# Revit family: AMB 162(182)_RFA_1
name_source: partatom
category: Pipe Accessories
units: mm (PartAtom-declared; Revit-internal decimal feet)

## family parameters
Always vertical = Yes
Cut with Voids When Loaded = No
OmniClass Number = 23.65.55.14.17
OmniClass Title = Adjusting/Controlling Valves for Liquid Services
Part Type = Normal
Round Connector Dimension = Use Diameter
Shared = Yes
Work Plane-Based = No

## types (22) — shared parameters
Body Material = Danfoss Plastic Dark Gray
Description = Gear Actuator
H = 101 mm  [stored 0.331365 ft]
IfcExportAs = IfcActuatorType
IfcExportType = AMB Actuator
L = 101 mm  [stored 0.331365 ft]
Manufacturer = Danfoss
Max Ambient Temperature = 50 °C
Max Medium Temperature = 110 °C
Min Ambient Temperature = 0 °C
URL = https://store.danfoss.com
W = 84 mm  [stored 0.275591 ft]

## per-type parameters (varying)
| type | Control Input Signal | For Rotary Valve DN | Model | Model Type | Operating Torque | Speed | Weight | With Auxiliary Switch |
| AMB 162_2-point_24V_15s/°_082H0270_082H0272 | 2-point | DN15-50 | 082H0270, 082H0272 | AMB 162_2-point_24V_15s/° | 5 Nm | 15 s/° | 0.70 kg | 082H0272 |
| AMB 162_3-point_230V_15s/°_082H0220_082H0225 | 3-point | DN15-50 | 082H0220, 082H0225 | AMB 162_3-point_230V_15s/° | 5 Nm | 15 s/° | 0.70 kg | 082H0225 |
| AMB 162_2-point_230V_15s/°_082H0271_082H0273 | 2-point | DN15-50 | 082H0271, 082H0273 | AMB 162_2-point_230V_15s/° | 5 Nm | 15 s/° | 0.70 kg | 082H0273 |
| AMB 162_3-point_24V_15s/°_082H0210_082H0215 | 3-point | DN15-50 | 082H0210, 082H0215 | AMB 162_3-point_24V_15s/°_ | 5 Nm | 15 s/° | 0.70 kg | 082H0215 |
| AMB 162_3-point_24V_30s/°_082H0211_082H0216 | 3-point | DN15-50 | 082H0211, 082H0216 | AMB 162_3-point_24V_30s/° | 5 Nm | 30 s/° | 0.70 kg | 082H0216 |
| AMB 162_3-point_24V_60s/°_082H0212_082H0217 | 3-point | DN15-50 | 082H0212, 082H0217 | AMB 162_3-point_24V_60s/° | 5 Nm | 60 s/° | 0.70 kg | 082H0217 |
| AMB 162_3-point_24V_120s/°_082H0213_082H0218 | 3-point | DN15-50 | 082H0213, 082H0218 | AMB 162_3-point_24V_120s/° | 5 Nm | 120 s/° | 0.70 kg | 082H0218 |
| AMB 162_3-point_24V_480s/°_082H0214_082H0219 | 3-point | DN15-50 | 082H0214, 082H0219 | AMB 162_3-point_24V_480s/° | 5 Nm | 120 s/° | 0.70 kg | 082H0219 |
| AMB 162_3-point_230V_30s/°_082H0221_082H0226 | 3-point | DN15-50 | 082H0221, 082H0226 | AMB 162_3-point_230V_30s/° | 5 Nm | 30 s/° | 0.70 kg | 082H0226 |
| AMB 162_3-point_230V_60s/°_082H0222_082H0227 | 3-point | DN15-50 | 082H0222, 082H0227 | AMB 162_3-point_230V_60s/° | 5 Nm | 60 s/° | 0.70 kg | 082H0227 |
| AMB 162_3-point_230V_120s/°_082H0223_082H0228 | 3-point | DN15-50 | 082H0223, 082H0228 | AMB 162_3-point_230V_120s/° | 5 Nm | 120 s/° | 0.70 kg | 082H0228 |
| AMB 162_3-point_230V_480s/°_082H0224_082H0229 | 3-point | DN15-50 | 082H0224, 082H0229 | AMB 162_3-point_230V_480s/° | 5 Nm | 480 s/° | 0.70 kg | 082H0229 |
| AMB 162_Modulating_24V_60/90/120s/°_082H0230 | Modulating | DN15-50 | 082H0230 | AMB 162_Modulating_24V_60/90/120s/° | 5 Nm | 60/90/120 s/° | 0.70 kg |  |
| AMB 182_2-point_230V_60s/°_082H0275_082H0277 | 2-point | DN15-150 | 082H0275, 082H0277 | AMB 182_2-point_230V_60s/° | 15 Nm | 60 s/° | 0.80 kg | 082H0277 |
| AMB 182_2-point_24V_60s/°_082H0274_082H0276 | 2-point | DN15-150 | 082H0274, 082H0276 | AMB 182_2-point_24V_60s/° | 15 Nm | 60 s/° | 0.80 kg | 082H0276 |
| AMB 182_3-point_230V_60s/°_082H0237_082H0239 | 3-point | DN15-150 | 082H0237, 082H0239 | AMB 182_3-point_230V_60s/° | 15 Nm | 60 s/° | 0.80 kg | 082H0239 |
| AMB 182_3-point_24V_60s/°_082H0233_082H0235 | 3-point | DN15-150 | 082H0233, 082H0235 | AMB 182_3-point_24V_60s/° | 15 Nm | 60 s/° | 0.80 kg | 082H0235 |
| AMB 182_3-point_24V_60s/°_10Nm_082H0231 | 3-point | DN15-100 | 082H0231 | AMB 182_3-point_24V_60s/°_10Nm | 10 Nm | 60 s/° | 0.80 kg |  |
| AMB 182_3-point_230V_60s/°_10Nm_082H0232 | 3-point | DN15-100 | 082H0232 | AMB 182_3-point_230V_60s/°_10Nm | 10 Nm | 60 s/° | 0.80 kg |  |
| AMB 182_3-point_24V_240s/°_082H0234_082H0236 | 3-point | DN15-150 | 082H0234, 082H0236 | AMB 182_3-point_24V_240s/° | 15 Nm | 240 s/° | 0.80 kg | 082H0236 |
| AMB 182_3-point_230V_240s/°_082H0238_082H0240 | 3-point | DN15-150 | 082H0238, 082H0240 | AMB 182_3-point_230V_240s/° | 15 Nm | 240 s/° | 0.80 kg | 082H0240 |
| AMB 182_Modulating_24V_60/90/120s/°_082H0241 | Modulating | DN15-150 | 082H0241 | AMB 182_Modulating_24V_60/90/120s/° | 15 Nm | 60/90/120 s/° | 0.80 kg |  |

note: [stored X ft] marks values corroborated as IEEE doubles in the binary element streams (Revit-internal decimal feet)

## geometry (parser evidence)
native form markers: Sweep x3
no freeform markers — native parametric forms only
